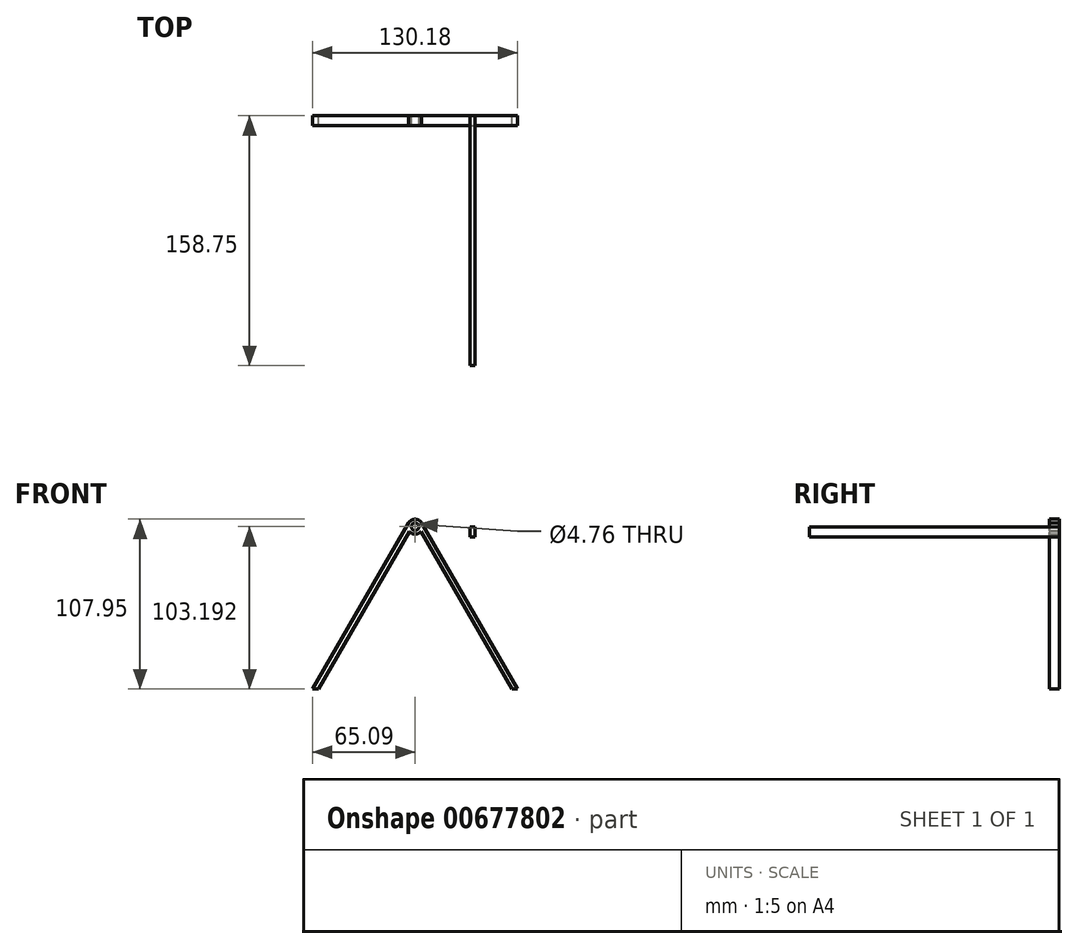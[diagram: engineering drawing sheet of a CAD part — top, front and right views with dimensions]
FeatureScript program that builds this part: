
annotation { "Feature Type Name" : "Feature", "Feature Type Description" : "" }
export const myFeature = defineFeature(function(context is Context, id is Id, definition is map)
    precondition{}
    {
        {
            var Q0;
            Q0=qCreatedBy(makeId("Front.planeOp"),FACE);
            var sketch = newSketch(context, id + "F0", { "sketchPlane" : qUnion([Q0])});
            skCircle(sketch, "E0.cCircle", {"center": v(0, -2.69) * mm, "radius": 37.58 * mm, "construction": true});
            skLineSegment(sketch, "E0.0", {"start": v(65.09, -40.27) * mm, "end": v(-65.09, -40.27) * mm});
            skLineSegment(sketch, "E0.1", {"start": v(-65.09, -40.27) * mm, "end": v(-4.08, 65.4) * mm});
            skLineSegment(sketch, "E0.2", {"start": v(4.11, 65.34) * mm, "end": v(65.09, -40.27) * mm});
            skPoint(sketch, "E0.0.midPoint", {"position": v(0, -40.27) * mm});
            skCircle(sketch, "E1", {"center": v(0, 62.92) * mm, "radius": 2.38 * mm});
            skCircle(sketch, "E2", {"center": v(0, 62.92) * mm, "radius": 4.76 * mm});
            skLineSegment(sketch, "E3", {"start": v(0, -40.27) * mm, "end": v(0, 72.47) * mm, "construction": true});
            skLineSegment(sketch, "E4", {"start": v(-61.42, -40.27) * mm, "end": v(-3.63, 59.84) * mm});
            skLineSegment(sketch, "E5.MirrorCS", {"start": v(61.42, -40.27) * mm, "end": v(3.63, 59.84) * mm});
            skArc(sketch, "E6", {"start": v(4.18, 65.24) * mm, "mid": v(-0.04, 67.68) * mm, "end": v(-4.21, 65.17) * mm});
            skPoint(sketch, "E6.first.point", {"position": v(-4.21, 65.17) * mm});
            skPoint(sketch, "E6.second.point", {"position": v(4.18, 65.24) * mm});
            skPoint(sketch, "E6.third.point", {"position": v(0, 67.68) * mm});
            skLineSegment(sketch, "E7.bottom", {"start": v(34.74, 62.66) * mm, "end": v(37.92, 62.66) * mm});
            skLineSegment(sketch, "E7.top", {"start": v(34.74, 56.31) * mm, "end": v(37.92, 56.31) * mm});
            skLineSegment(sketch, "E7.left", {"start": v(34.74, 62.66) * mm, "end": v(34.74, 56.31) * mm});
            skLineSegment(sketch, "E7.right", {"start": v(37.92, 62.66) * mm, "end": v(37.92, 56.31) * mm});
            skSolve(sketch);
        }
        {
            var Q0;
            Q0=makeQuery(id+"F0.imprint","IMPRINT",FACE,{"disambiguationData":[TD([[makeQuery(id+"F0.imprint","IMPRINT",EDGE,{"derivedFrom":sQuery(id+"F0.wireOp",EDGE,"E1")}),-1.0]])]});
            var Q1;
            {var subQ4=sQuery(id+"F0.wireOp",EDGE,"E0.2");Q1=makeQuery(id+"F0.imprint","IMPRINT",FACE,{"disambiguationData":[TD([[makeQuery(id+"F0.imprint","IMPRINT",EDGE,{"derivedFrom":subQ4}),-1.0]])]});}
            var Q2;
            {var subQ4=sQuery(id+"F0.wireOp",EDGE,"E4");Q2=makeQuery(id+"F0.imprint","IMPRINT",FACE,{"disambiguationData":[TD([[makeQuery(id+"F0.imprint","IMPRINT",EDGE,{"derivedFrom":subQ4}),1.0]])]});}
            extrude(context, id + "F1", {"entities" : qUnion([Q0, Q1, Q2]), "depth" : 6.35 * mm, "offsetDistance" : 25.4 * mm});
        }
        {
            var Q0;
            Q0=makeQuery(id+"F0.imprint","IMPRINT",FACE,{"disambiguationData":[TD([[makeQuery(id+"F0.imprint","IMPRINT",EDGE,{"derivedFrom":sQuery(id+"F0.wireOp",EDGE,"E7.bottom")}),-1.0]])]});
            extrude(context, id + "F2", {"entities" : qUnion([Q0]), "depth" : 158.75 * mm, "offsetDistance" : 25.4 * mm});
        }
    });
